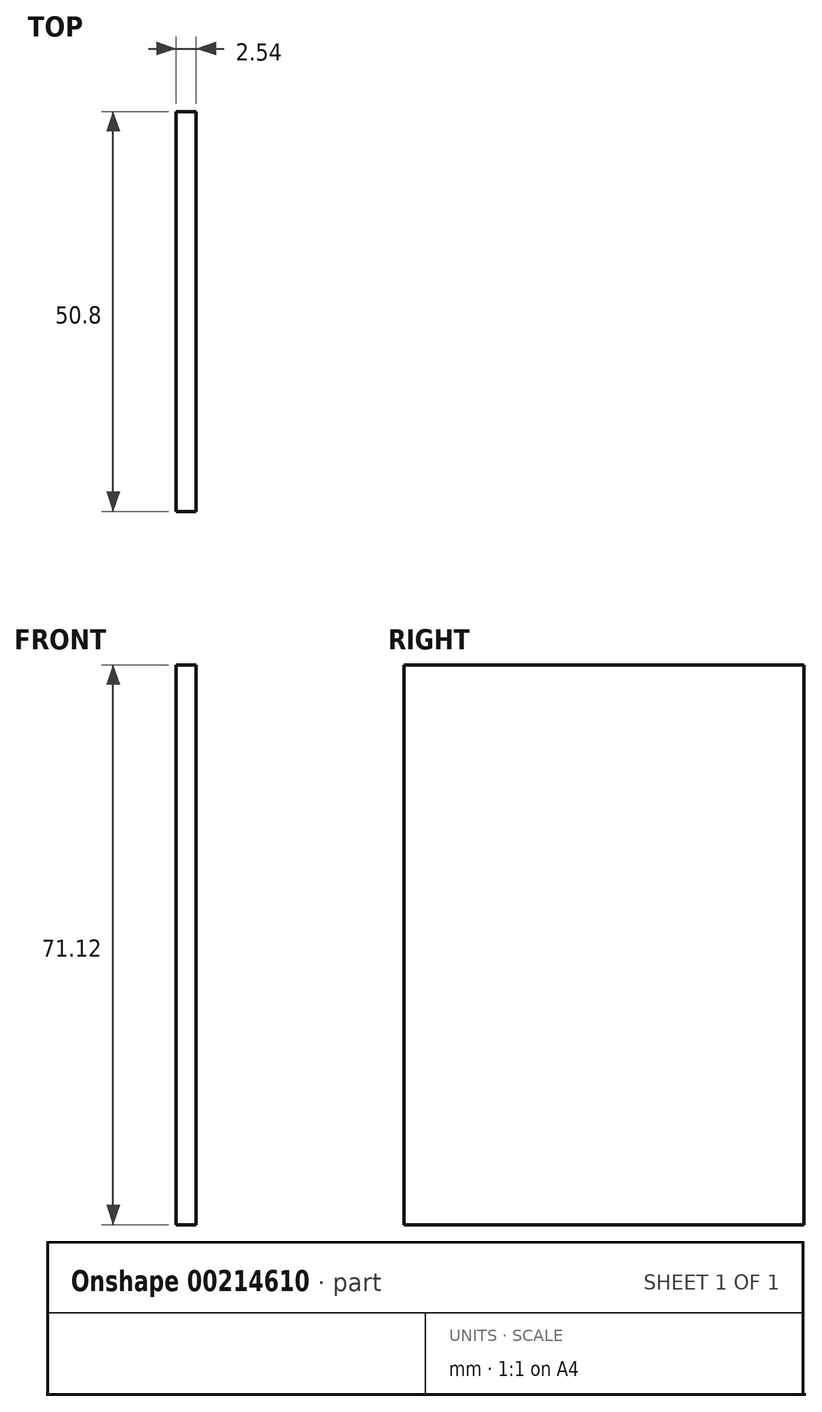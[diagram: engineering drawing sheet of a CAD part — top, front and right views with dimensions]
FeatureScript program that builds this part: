
annotation { "Feature Type Name" : "Feature", "Feature Type Description" : "" }
export const myFeature = defineFeature(function(context is Context, id is Id, definition is map)
    precondition{}
    {
        {
            var Q0;
            Q0=qCreatedBy(makeId("Right.planeOp"),FACE);
            var sketch = newSketch(context, id + "F0", { "sketchPlane" : qUnion([Q0])});
            skLineSegment(sketch, "E0.bottom", {"start": v(-23.96, 48.72) * mm, "end": v(26.84, 48.72) * mm});
            skLineSegment(sketch, "E0.top", {"start": v(-23.96, -22.4) * mm, "end": v(26.84, -22.4) * mm});
            skLineSegment(sketch, "E0.left", {"start": v(-23.96, 48.72) * mm, "end": v(-23.96, -22.4) * mm});
            skLineSegment(sketch, "E0.right", {"start": v(26.84, 48.72) * mm, "end": v(26.84, -22.4) * mm});
            skSolve(sketch);
        }
        {
            var Q0;
            Q0=makeQuery(id+"F0.imprint","IMPRINT",FACE,{"disambiguationData":[TD([[makeQuery(id+"F0.imprint","IMPRINT",EDGE,{"derivedFrom":sQuery(id+"F0.wireOp",EDGE,"E0.bottom")}),-1.0]])]});
            extrude(context, id + "F1", {"entities" : qUnion([Q0]), "depth" : 2.54 * mm});
        }
    });
